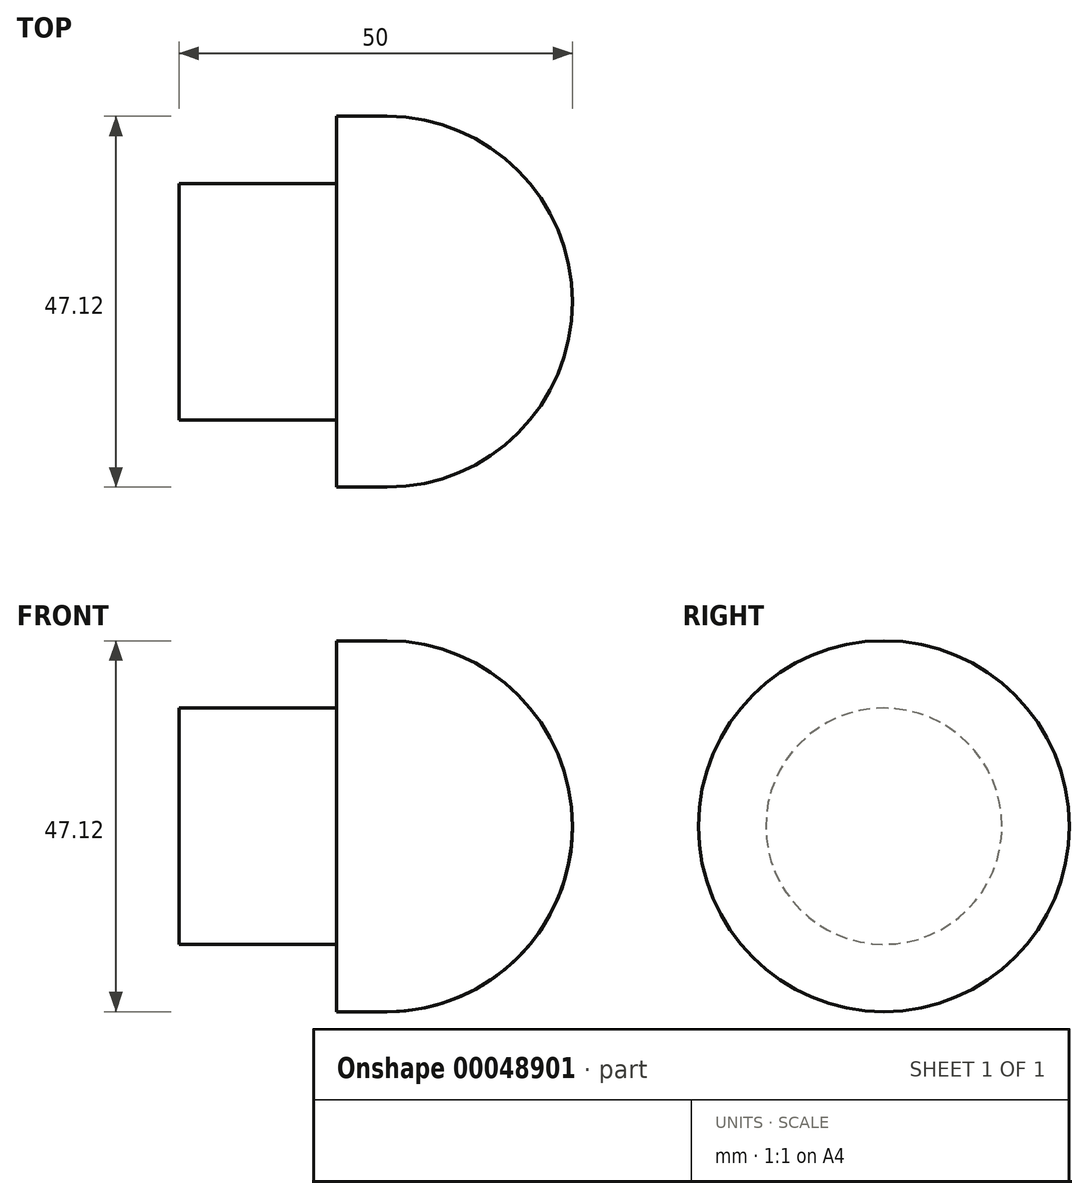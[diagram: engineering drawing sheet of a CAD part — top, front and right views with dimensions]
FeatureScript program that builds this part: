
annotation { "Feature Type Name" : "Feature", "Feature Type Description" : "" }
export const myFeature = defineFeature(function(context is Context, id is Id, definition is map)
    precondition{}
    {
        {
            var Q0;
            Q0=qCreatedBy(makeId("Front.planeOp"),FACE);
            var sketch = newSketch(context, id + "F0", { "sketchPlane" : qUnion([Q0])});
            skLineSegment(sketch, "E0", {"start": v(6.94, 23.56) * mm, "end": v(0.5, 23.56) * mm});
            skLineSegment(sketch, "E1", {"start": v(-19.5, 0) * mm, "end": v(-19.5, 15) * mm});
            skLineSegment(sketch, "E2", {"start": v(-19.5, 15) * mm, "end": v(0.5, 15) * mm});
            skLineSegment(sketch, "E3", {"start": v(0.5, 15) * mm, "end": v(0.5, 23.56) * mm});
            skArc(sketch, "E4", {"start": v(6.94, 23.56) * mm, "mid": v(23.6, 16.66) * mm, "end": v(30.5, 0) * mm});
            skLineSegment(sketch, "E5", {"start": v(-19.5, 0) * mm, "end": v(30.5, 0) * mm});
            skSolve(sketch);
        }
        {
            var Q0;
            Q0=makeQuery(id+"F0.imprint","IMPRINT",FACE,{"disambiguationData":[TD([[makeQuery(id+"F0.imprint","IMPRINT",EDGE,{"derivedFrom":sQuery(id+"F0.wireOp",EDGE,"E0")}),1.0]])]});
            var Q1;
            Q1=sQuery(id+"F0.wireOp",EDGE,"E5");
            revolve(context, id + "F1", {"entities" : qUnion([Q0]), "axis" : qUnion([Q1]), "revolveType" : RevolveType.FULL});
        }
    });
